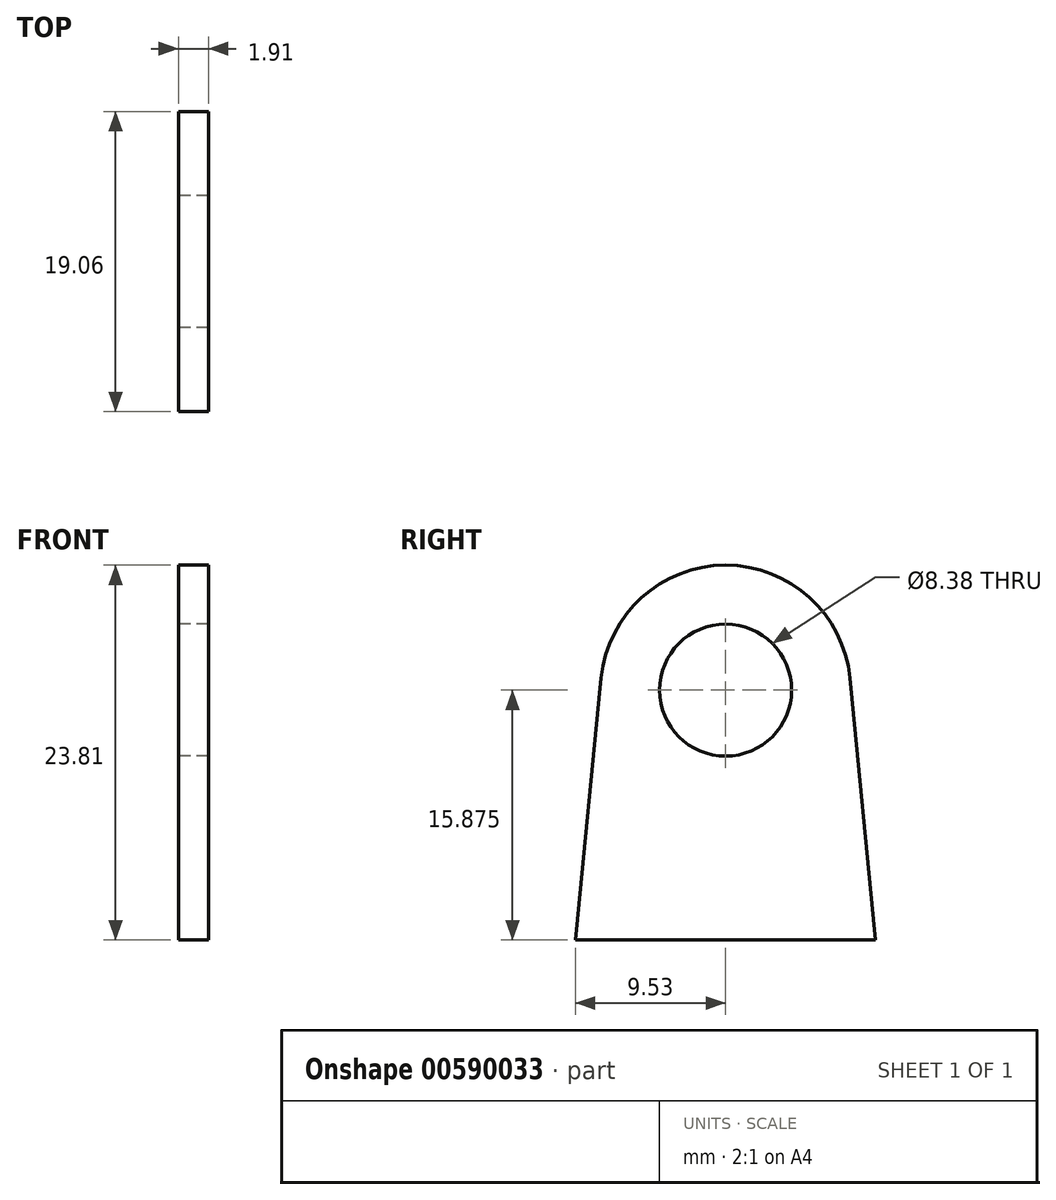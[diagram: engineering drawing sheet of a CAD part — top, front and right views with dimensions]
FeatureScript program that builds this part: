
annotation { "Feature Type Name" : "Feature", "Feature Type Description" : "" }
export const myFeature = defineFeature(function(context is Context, id is Id, definition is map)
    precondition{}
    {
        {
            var Q0;
            Q0=qCreatedBy(makeId("Right.planeOp"),FACE);
            var sketch = newSketch(context, id + "F0", { "sketchPlane" : qUnion([Q0])});
            skCircle(sketch, "E0", {"center": v(0, 15.88) * mm, "radius": 4.2 * mm});
            skArc(sketch, "E1", {"start": v(7.9, 16.65) * mm, "mid": v(0, 23.81) * mm, "end": v(-7.9, 16.65) * mm});
            skLineSegment(sketch, "E2", {"start": v(-9.53, 0) * mm, "end": v(-7.9, 16.65) * mm});
            skLineSegment(sketch, "E3", {"start": v(-9.53, 0) * mm, "end": v(9.53, 0) * mm});
            skLineSegment(sketch, "E4", {"start": v(9.53, 0) * mm, "end": v(7.9, 16.65) * mm});
            skSolve(sketch);
        }
        {
            var Q0;
            Q0 = qSketchRegion(id + "F0", true);
            extrude(context, id + "F1", {"entities" : qUnion([Q0]), "depth" : 1.9 * mm, "offsetDistance" : 25.4 * mm});
        }
    });
